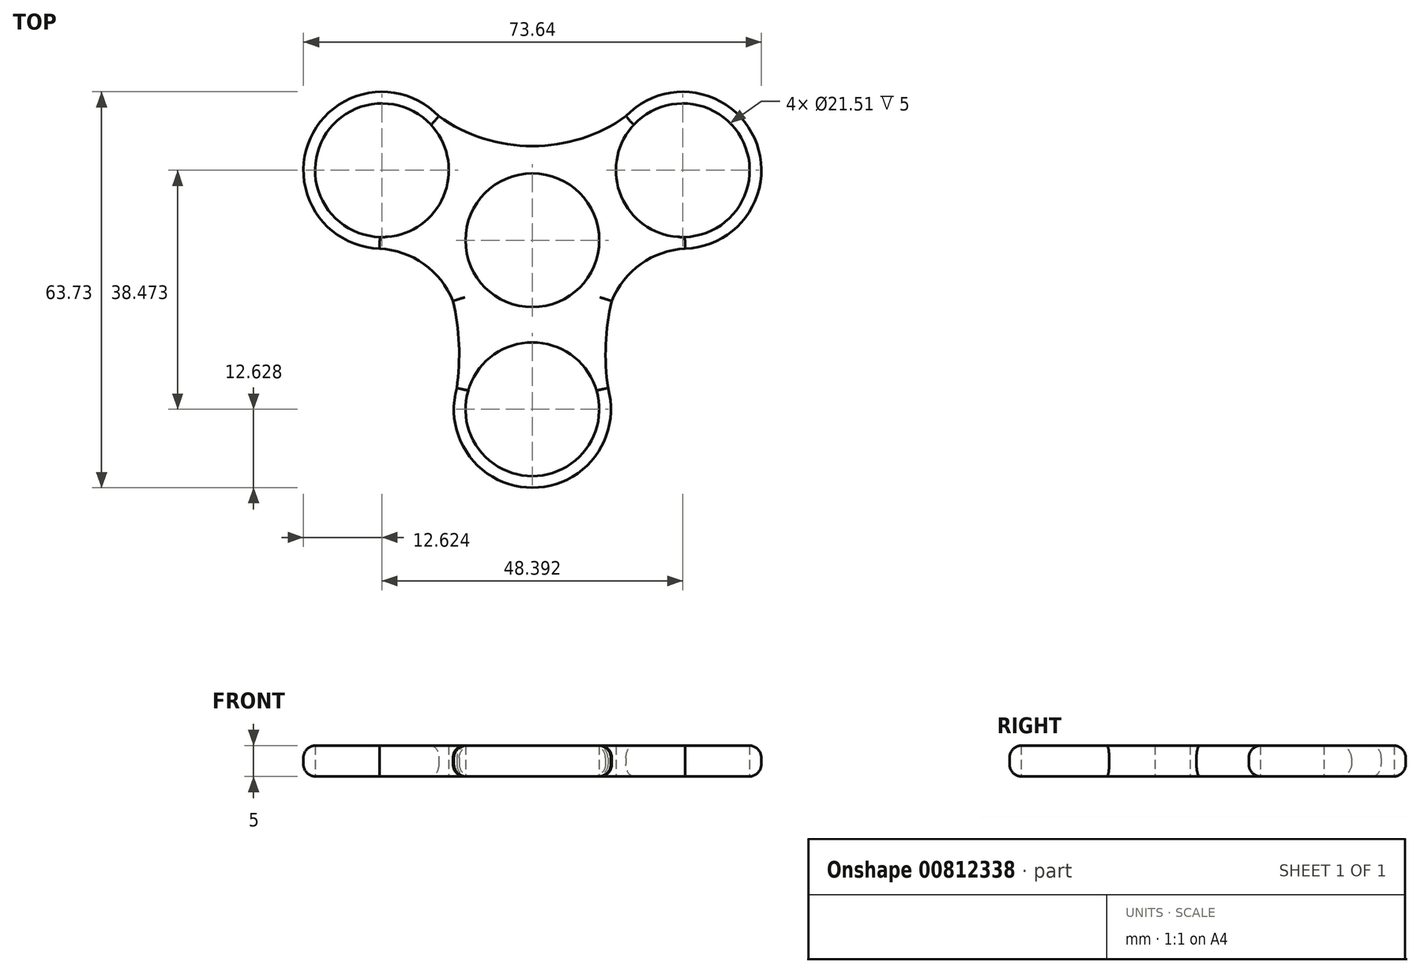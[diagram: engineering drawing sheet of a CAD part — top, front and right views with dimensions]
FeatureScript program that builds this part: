
annotation { "Feature Type Name" : "Feature", "Feature Type Description" : "" }
export const myFeature = defineFeature(function(context is Context, id is Id, definition is map)
    precondition{}
    {
        {
            var Q0;
            Q0=qCreatedBy(makeId("Top.planeOp"),FACE);
            var sketch = newSketch(context, id + "F0", { "sketchPlane" : qUnion([Q0])});
            skCircle(sketch, "E0", {"center": v(0, 0) * mm, "radius": 10.75 * mm});
            skCircle(sketch, "E1", {"center": v(24.2, 11.27) * mm, "radius": 10.75 * mm});
            skCircle(sketch, "E2", {"center": v(0, -27.2) * mm, "radius": 10.75 * mm});
            skCircle(sketch, "E3", {"center": v(24.2, 11.27) * mm, "radius": 12.63 * mm});
            skCircle(sketch, "E4", {"center": v(0, -27.2) * mm, "radius": 12.63 * mm});
            skCircle(sketch, "E5.MirrorC", {"center": v(-24.2, 11.27) * mm, "radius": 12.63 * mm});
            skCircle(sketch, "E6.MirrorC", {"center": v(-24.2, 11.27) * mm, "radius": 10.75 * mm});
            skArc(sketch, "E7", {"start": v(-17.54, 22) * mm, "mid": v(-9.41, 16.93) * mm, "end": v(0, 15.18) * mm});
            skArc(sketch, "E8", {"start": v(-12.77, -9.77) * mm, "mid": v(-17.52, -3.76) * mm, "end": v(-24.78, -1.34) * mm});
            skArc(sketch, "E9", {"start": v(-12.16, -23.79) * mm, "mid": v(-11.8, -16.75) * mm, "end": v(-12.77, -9.77) * mm});
            skArc(sketch, "E10.MirrorCS", {"start": v(17.54, 22) * mm, "mid": v(9.41, 16.93) * mm, "end": v(0, 15.18) * mm});
            skArc(sketch, "E11.MirrorCS", {"start": v(12.77, -9.77) * mm, "mid": v(17.52, -3.76) * mm, "end": v(24.78, -1.34) * mm});
            skArc(sketch, "E12.MirrorCS", {"start": v(12.16, -23.79) * mm, "mid": v(11.8, -16.75) * mm, "end": v(12.77, -9.77) * mm});
            skSolve(sketch);
        }
        {
            var Q0;
            Q0 = qSketchRegion(id + "F0", true);
            extrude(context, id + "F1", {"entities" : qUnion([Q0]), "depth" : 5 * mm, "offsetDistance" : 25 * mm});
        }
        {
            var Q0;
            Q0=makeQuery(id+"F1.opExtrude","CAP_EDGE",EDGE,{"disambiguationData":[OSD([sQuery(id+"F0.wireOp",EDGE,"E9")])],"isStart":true});
            var Q1;
            Q1=makeQuery(id+"F1.opExtrude","CAP_EDGE",EDGE,{"disambiguationData":[OSD([sQuery(id+"F0.wireOp",EDGE,"E4")])],"isStart":true});
            var Q2;
            Q2=makeQuery(id+"F1.opExtrude","CAP_EDGE",EDGE,{"disambiguationData":[OSD([sQuery(id+"F0.wireOp",EDGE,"E8")])],"isStart":true});
            var Q3;
            Q3=makeQuery(id+"F1.opExtrude","CAP_EDGE",EDGE,{"disambiguationData":[OSD([sQuery(id+"F0.wireOp",EDGE,"E7")])],"isStart":true});
            var Q4;
            Q4=makeQuery(id+"F1.opExtrude","CAP_EDGE",EDGE,{"disambiguationData":[OSD([sQuery(id+"F0.wireOp",EDGE,"E10.MirrorCS")])],"isStart":true});
            var Q5;
            Q5=makeQuery(id+"F1.opExtrude","CAP_EDGE",EDGE,{"disambiguationData":[OSD([sQuery(id+"F0.wireOp",EDGE,"E11.MirrorCS")])],"isStart":true});
            var Q6;
            Q6=makeQuery(id+"F1.opExtrude","CAP_EDGE",EDGE,{"disambiguationData":[OSD([sQuery(id+"F0.wireOp",EDGE,"E12.MirrorCS")])],"isStart":true});
            var Q7;
            Q7=makeQuery(id+"F1.opExtrude","CAP_EDGE",EDGE,{"disambiguationData":[OSD([sQuery(id+"F0.wireOp",EDGE,"E3")])],"isStart":true});
            var Q8;
            Q8=makeQuery(id+"F1.opExtrude","CAP_EDGE",EDGE,{"disambiguationData":[OSD([sQuery(id+"F0.wireOp",EDGE,"E5.MirrorC")])],"isStart":true});
            fillet(context, id + "F2", {"entities" : qUnion([Q0, Q1, Q2, Q3, Q4, Q5, Q6, Q7, Q8]), "radius" : 2 * mm, "tangentPropagation" : true, "allowEdgeOverflow" : false});
        }
        {
            var Q0;
            Q0=makeQuery(id+"F1.opExtrude","CAP_EDGE",EDGE,{"disambiguationData":[OSD([sQuery(id+"F0.wireOp",EDGE,"E7")])],"isStart":false});
            var Q1;
            Q1=makeQuery(id+"F1.opExtrude","CAP_EDGE",EDGE,{"disambiguationData":[OSD([sQuery(id+"F0.wireOp",EDGE,"E10.MirrorCS")])],"isStart":false});
            var Q2;
            Q2=makeQuery(id+"F1.opExtrude","CAP_EDGE",EDGE,{"disambiguationData":[OSD([sQuery(id+"F0.wireOp",EDGE,"E11.MirrorCS")])],"isStart":false});
            var Q3;
            Q3=makeQuery(id+"F1.opExtrude","CAP_EDGE",EDGE,{"disambiguationData":[OSD([sQuery(id+"F0.wireOp",EDGE,"E12.MirrorCS")])],"isStart":false});
            var Q4;
            Q4=makeQuery(id+"F1.opExtrude","CAP_EDGE",EDGE,{"disambiguationData":[OSD([sQuery(id+"F0.wireOp",EDGE,"E9")])],"isStart":false});
            var Q5;
            Q5=makeQuery(id+"F1.opExtrude","CAP_EDGE",EDGE,{"disambiguationData":[OSD([sQuery(id+"F0.wireOp",EDGE,"E5.MirrorC")])],"isStart":false});
            var Q6;
            Q6=makeQuery(id+"F1.opExtrude","CAP_EDGE",EDGE,{"disambiguationData":[OSD([sQuery(id+"F0.wireOp",EDGE,"E4")])],"isStart":false});
            var Q7;
            Q7=makeQuery(id+"F1.opExtrude","CAP_EDGE",EDGE,{"disambiguationData":[OSD([sQuery(id+"F0.wireOp",EDGE,"E3")])],"isStart":false});
            var Q8;
            Q8=makeQuery(id+"F1.opExtrude","CAP_EDGE",EDGE,{"disambiguationData":[OSD([sQuery(id+"F0.wireOp",EDGE,"E8")])],"isStart":false});
            fillet(context, id + "F3", {"entities" : qUnion([Q0, Q1, Q2, Q3, Q4, Q5, Q6, Q7, Q8]), "radius" : 2 * mm, "tangentPropagation" : true, "allowEdgeOverflow" : false});
        }
    });
